# Revit family: Basin-Ligature_Resistant-Whitehall-BestCare-WH3740_Series
name_source: partatom
category: Plumbing Fixtures
units: mm (PartAtom-declared; Revit-internal decimal feet)

## family parameters
Cut with Voids When Loaded = No
Host = Face
OmniClass Number = 23.45.05.14.14
OmniClass Title = Sinks/Lavatories
Part Type = Normal
Room Calculation Point = No
Round Connector Dimension = Use Diameter
Shared = Yes

## types (4) — shared parameters
ADA Compliant = Yes
CW Connection = Yes
CWFU = 1.5
Compliance Certifications = UPC®, Federal Public Law 111-380 - No Lead
Connection Size = 1/2"
Default Elevation = 34"
Description = BestCare® Ligature-Resistant Stainless Steel Basin
HW Connection = Yes
HWFU = 1.5
Height = 25 1/4"
Installation Type = Wall Mounted
Length = 19"
MC Mounting Carrier = No
Manufacturer = Whitehall Mfg
Product Documentation Link = https://www.whitehallmfg.com
Product Page URL = https://www.whitehallmfg.com
URL = http://www.whitehallmfg.com
Vent Connection = No
WFU = 2
WHST70-12 1/2” NPT ASSE 1070 Compliant Hot & Cold, Temperature / Pressure Balancing Mixing Valve = No
Waste Connection = Yes
Waste Connection Diameter = 1 1/2"
Width = 21 1/2"

## per-type parameters (varying)
| type | Finish | Left Faucet Hole Distance | Material | Right Faucet Hole Distance | Type Comments |
| WH3740 | Stainless Steel-Whitehall-Powder Coated White | 2" | Stainless Steel-Whitehall-Powder Coated White | 2" | Ligature Resistant Stainless Steel Washbasin (Punched for 4” Centerset Faucet, Specified Separately) |
| WH3740-H38 | Stainless Steel-Whitehall-Powder Coated White | 4" | Stainless Steel-Whitehall-Powder Coated White | 4" | Ligature Resistant Stainless Steel Washbasin (Punched for 8” Centerset Faucet, Specified Separately) |
| WH3740-SS | Stainless Steel-Whitehall-Satin | 2" | Stainless Steel-Whitehall-Satin | 2" | LR Washbasin-#4 Stainless Steel Finish (Punched for 4” Centerset Faucet, Spec. Separately) |
| WH3740-H38-SS | Stainless Steel-Whitehall-Satin | 4" | Stainless Steel-Whitehall-Satin | 4" | LR Washbasin-#4 Stainless Steel Finish (Punched for 8” Centerset Faucet, Spec. Separately) |

note: column(s) folded — value = type name in every type: Model

## geometry (parser evidence)
native form markers: Sweep x3
no freeform markers — native parametric forms only
